annotation { "Feature Type Name" : "Feature", "Feature Type Description" : "" }
export const myFeature = defineFeature(function(context is Context, id is Id, definition is map)
    precondition{}
    {
        {
            var Q0;
            Q0=qCreatedBy(makeId("Top.planeOp"),FACE);
            var sketch = newSketch(context, id + "F0", { "sketchPlane" : qUnion([Q0])});
            skLineSegment(sketch, "E0.bottom", {"start": v(-40, 25) * mm, "end": v(40, 25) * mm});
            skLineSegment(sketch, "E0.top", {"start": v(-40, -25) * mm, "end": v(40, -25) * mm});
            skLineSegment(sketch, "E0.left", {"start": v(-40, 25) * mm, "end": v(-40, -25) * mm});
            skLineSegment(sketch, "E0.right", {"start": v(40, 25) * mm, "end": v(40, -25) * mm});
            skPoint(sketch, "E0.middle", {"position": v(0, 0) * mm});
            skSolve(sketch);
        }
        {
            var Q0;
            Q0 = qSketchRegion(id + "F0", true);
            extrude(context, id + "F1", {"entities" : qUnion([Q0]), "depth" : 100 * mm, "offsetDistance" : 25 * mm});
        }
        {
            var Q0;
            Q0=makeQuery(id+"F1.opExtrude","CAP_FACE",FACE,{"disambiguationData":[OSD([sQuery(id+"F0.wireOp",EDGE,"E0.bottom"),sQuery(id+"F0.wireOp",EDGE,"E0.top"),sQuery(id+"F0.wireOp",EDGE,"E0.left"),sQuery(id+"F0.wireOp",EDGE,"E0.right")])],"isStart":false});
            shell(context, id + "F2", {"entities" : qUnion([Q0]), "thickness" : 2.5 * mm});
        }
        {
            var Q0;
            Q0=makeQuery(id+"F1.opExtrude","CAP_FACE",FACE,{"disambiguationData":[OSD([sQuery(id+"F0.wireOp",EDGE,"E0.bottom"),sQuery(id+"F0.wireOp",EDGE,"E0.top"),sQuery(id+"F0.wireOp",EDGE,"E0.left"),sQuery(id+"F0.wireOp",EDGE,"E0.right")])],"isStart":true});
            var sketch = newSketch(context, id + "F3", { "sketchPlane" : qUnion([Q0])});
            skLineSegment(sketch, "E1", {"start": v(0, 19.4) * mm, "end": v(0, -22.73) * mm, "construction": true});
            skLineSegment(sketch, "E2", {"start": v(-35.25, 0) * mm, "end": v(36.43, 0) * mm, "construction": true});
            skLineSegment(sketch, "E3.bottom", {"start": v(-41, 26) * mm, "end": v(-11, 26) * mm});
            skLineSegment(sketch, "E3.top", {"start": v(-41, 6) * mm, "end": v(-11, 6) * mm});
            skLineSegment(sketch, "E3.left", {"start": v(-41, 26) * mm, "end": v(-41, 6) * mm});
            skLineSegment(sketch, "E3.right", {"start": v(-11, 26) * mm, "end": v(-11, 6) * mm});
            skLineSegment(sketch, "E4.bottom", {"start": v(-42, 27) * mm, "end": v(-16, 27) * mm});
            skLineSegment(sketch, "E4.top", {"start": v(-42, 11) * mm, "end": v(-16, 11) * mm});
            skLineSegment(sketch, "E4.left", {"start": v(-42, 27) * mm, "end": v(-42, 11) * mm});
            skLineSegment(sketch, "E4.right", {"start": v(-16, 27) * mm, "end": v(-16, 11) * mm});
            skLineSegment(sketch, "E5.bottom", {"start": v(-43, 28) * mm, "end": v(-21, 28) * mm});
            skLineSegment(sketch, "E5.top", {"start": v(-43, 16) * mm, "end": v(-21, 16) * mm});
            skLineSegment(sketch, "E5.left", {"start": v(-43, 28) * mm, "end": v(-43, 16) * mm});
            skLineSegment(sketch, "E5.right", {"start": v(-21, 28) * mm, "end": v(-21, 16) * mm});
            skLineSegment(sketch, "E6.MirrorCS", {"start": v(21, 28) * mm, "end": v(21, 16) * mm});
            skLineSegment(sketch, "E7.MirrorCS", {"start": v(41, 6) * mm, "end": v(11, 6) * mm});
            skLineSegment(sketch, "E8.MirrorCS", {"start": v(41, 26) * mm, "end": v(41, 6) * mm});
            skLineSegment(sketch, "E9.MirrorCS", {"start": v(11, 26) * mm, "end": v(11, 6) * mm});
            skLineSegment(sketch, "E10.MirrorCS", {"start": v(42, 27) * mm, "end": v(16, 27) * mm});
            skLineSegment(sketch, "E11.MirrorCS", {"start": v(42, 11) * mm, "end": v(16, 11) * mm});
            skLineSegment(sketch, "E12.MirrorCS", {"start": v(42, 27) * mm, "end": v(42, 11) * mm});
            skLineSegment(sketch, "E13.MirrorCS", {"start": v(41, 26) * mm, "end": v(11, 26) * mm});
            skLineSegment(sketch, "E14.MirrorCS", {"start": v(16, 27) * mm, "end": v(16, 11) * mm});
            skLineSegment(sketch, "E15.MirrorCS", {"start": v(43, 16) * mm, "end": v(21, 16) * mm});
            skLineSegment(sketch, "E16.MirrorCS", {"start": v(43, 28) * mm, "end": v(21, 28) * mm});
            skLineSegment(sketch, "E17.MirrorCS", {"start": v(43, 28) * mm, "end": v(43, 16) * mm});
            skLineSegment(sketch, "E18.MirrorCS", {"start": v(35.25, 0) * mm, "end": v(-36.43, 0) * mm, "construction": true});
            skLineSegment(sketch, "E19.MirrorCS", {"start": v(-21, -28) * mm, "end": v(-21, -16) * mm});
            skLineSegment(sketch, "E20.MirrorCS", {"start": v(-41, -26) * mm, "end": v(-11, -26) * mm});
            skLineSegment(sketch, "E21.MirrorCS", {"start": v(-41, -6) * mm, "end": v(-11, -6) * mm});
            skLineSegment(sketch, "E22.MirrorCS", {"start": v(-42, -27) * mm, "end": v(-16, -27) * mm});
            skLineSegment(sketch, "E23.MirrorCS", {"start": v(-11, -26) * mm, "end": v(-11, -6) * mm});
            skLineSegment(sketch, "E24.MirrorCS", {"start": v(-42, -11) * mm, "end": v(-16, -11) * mm});
            skLineSegment(sketch, "E25.MirrorCS", {"start": v(-42, -27) * mm, "end": v(-42, -11) * mm});
            skLineSegment(sketch, "E26.MirrorCS", {"start": v(-41, -26) * mm, "end": v(-41, -6) * mm});
            skLineSegment(sketch, "E27.MirrorCS", {"start": v(-16, -27) * mm, "end": v(-16, -11) * mm});
            skLineSegment(sketch, "E28.MirrorCS", {"start": v(-43, -28) * mm, "end": v(-21, -28) * mm});
            skLineSegment(sketch, "E29.MirrorCS", {"start": v(-43, -16) * mm, "end": v(-21, -16) * mm});
            skLineSegment(sketch, "E30.MirrorCS", {"start": v(-43, -28) * mm, "end": v(-43, -16) * mm});
            skLineSegment(sketch, "E31.MirrorCS", {"start": v(43, -28) * mm, "end": v(21, -28) * mm});
            skLineSegment(sketch, "E32.MirrorCS", {"start": v(41, -6) * mm, "end": v(11, -6) * mm});
            skLineSegment(sketch, "E33.MirrorCS", {"start": v(21, -28) * mm, "end": v(21, -16) * mm});
            skLineSegment(sketch, "E34.MirrorCS", {"start": v(42, -11) * mm, "end": v(16, -11) * mm});
            skLineSegment(sketch, "E35.MirrorCS", {"start": v(16, -27) * mm, "end": v(16, -11) * mm});
            skLineSegment(sketch, "E36.MirrorCS", {"start": v(41, -26) * mm, "end": v(41, -6) * mm});
            skLineSegment(sketch, "E37.MirrorCS", {"start": v(43, -28) * mm, "end": v(43, -16) * mm});
            skLineSegment(sketch, "E38.MirrorCS", {"start": v(11, -26) * mm, "end": v(11, -6) * mm});
            skLineSegment(sketch, "E39.MirrorCS", {"start": v(42, -27) * mm, "end": v(42, -11) * mm});
            skLineSegment(sketch, "E40.MirrorCS", {"start": v(42, -27) * mm, "end": v(16, -27) * mm});
            skLineSegment(sketch, "E41.MirrorCS", {"start": v(43, -16) * mm, "end": v(21, -16) * mm});
            skLineSegment(sketch, "E42.MirrorCS", {"start": v(41, -26) * mm, "end": v(11, -26) * mm});
            skSolve(sketch);
        }
        {
            var Q0;
            {var subQ1=sQuery(id+"F3.wireOp",EDGE,"E3.bottom");var subQ9=sQuery(id+"F3.wireOp",EDGE,"E3.left");var subQ11=makeQuery(id+"F3.imprint","INTERSECT",VERTEX,{"derivedFrom":[subQ1,subQ9]});Q0=makeQuery(id+"F3.imprint","IMPRINT",FACE,{"disambiguationData":[TD([[makeQuery(id+"F3.imprint","IMPRINT",EDGE,{"disambiguationData":[TD([[subQ11,-1.0]])],"derivedFrom":subQ1}),-1.0]])]});}
            var Q1;
            {var subQ0=sQuery(id+"F3.wireOp",EDGE,"E4.right");var subQ1=sQuery(id+"F3.wireOp",EDGE,"E3.bottom");var subQ2=makeQuery(id+"F3.imprint","INTERSECT",VERTEX,{"derivedFrom":[subQ1,subQ0]});Q1=makeQuery(id+"F3.imprint","IMPRINT",FACE,{"disambiguationData":[TD([[makeQuery(id+"F3.imprint","IMPRINT",EDGE,{"disambiguationData":[TD([[subQ2,1.0]])],"derivedFrom":subQ1}),-1.0]])]});}
            var Q2;
            {var subQ0=sQuery(id+"F3.wireOp",EDGE,"E3.right");var subQ1=sQuery(id+"F3.wireOp",EDGE,"E3.bottom");var subQ2=makeQuery(id+"F3.imprint","INTERSECT",VERTEX,{"derivedFrom":[subQ1,subQ0]});Q2=makeQuery(id+"F3.imprint","IMPRINT",FACE,{"disambiguationData":[TD([[makeQuery(id+"F3.imprint","IMPRINT",EDGE,{"disambiguationData":[TD([[subQ2,1.0]])],"derivedFrom":subQ1}),-1.0]])]});}
            var Q3;
            {var subQ0=sQuery(id+"F3.wireOp",EDGE,"E4.top");var subQ1=sQuery(id+"F3.wireOp",EDGE,"E3.left");var subQ2=makeQuery(id+"F3.imprint","INTERSECT",VERTEX,{"derivedFrom":[subQ1,subQ0]});Q3=makeQuery(id+"F3.imprint","IMPRINT",FACE,{"disambiguationData":[TD([[makeQuery(id+"F3.imprint","IMPRINT",EDGE,{"disambiguationData":[TD([[subQ2,1.0]])],"derivedFrom":subQ1}),1.0]])]});}
            var Q4;
            {var subQ0=sQuery(id+"F3.wireOp",EDGE,"E3.left");var subQ1=sQuery(id+"F3.wireOp",EDGE,"E3.top");var subQ2=makeQuery(id+"F3.imprint","INTERSECT",VERTEX,{"derivedFrom":[subQ1,subQ0]});Q4=makeQuery(id+"F3.imprint","IMPRINT",FACE,{"disambiguationData":[TD([[makeQuery(id+"F3.imprint","IMPRINT",EDGE,{"disambiguationData":[TD([[subQ2,-1.0]])],"derivedFrom":subQ1}),1.0]])]});}
            var Q5;
            {var subQ0=sQuery(id+"F3.wireOp",EDGE,"E26.MirrorCS");var subQ1=sQuery(id+"F3.wireOp",EDGE,"E21.MirrorCS");var subQ2=makeQuery(id+"F3.imprint","INTERSECT",VERTEX,{"derivedFrom":[subQ1,subQ0]});Q5=makeQuery(id+"F3.imprint","IMPRINT",FACE,{"disambiguationData":[TD([[makeQuery(id+"F3.imprint","IMPRINT",EDGE,{"disambiguationData":[TD([[subQ2,-1.0]])],"derivedFrom":subQ1}),-1.0]])]});}
            var Q6;
            {var subQ0=sQuery(id+"F3.wireOp",EDGE,"E26.MirrorCS");var subQ1=sQuery(id+"F3.wireOp",EDGE,"E24.MirrorCS");var subQ2=makeQuery(id+"F3.imprint","INTERSECT",VERTEX,{"derivedFrom":[subQ1,subQ0]});Q6=makeQuery(id+"F3.imprint","IMPRINT",FACE,{"disambiguationData":[TD([[makeQuery(id+"F3.imprint","IMPRINT",EDGE,{"disambiguationData":[TD([[subQ2,-1.0]])],"derivedFrom":subQ1}),-1.0]])]});}
            var Q7;
            {var subQ1=sQuery(id+"F3.wireOp",EDGE,"E20.MirrorCS");var subQ5=sQuery(id+"F3.wireOp",EDGE,"E19.MirrorCS");var subQ6=makeQuery(id+"F3.imprint","INTERSECT",VERTEX,{"derivedFrom":[subQ5,subQ1]});Q7=makeQuery(id+"F3.imprint","IMPRINT",FACE,{"disambiguationData":[TD([[makeQuery(id+"F3.imprint","IMPRINT",EDGE,{"disambiguationData":[TD([[subQ6,-1.0]])],"derivedFrom":subQ5}),1.0]])]});}
            var Q8;
            {var subQ0=sQuery(id+"F3.wireOp",EDGE,"E20.MirrorCS");var subQ1=sQuery(id+"F3.wireOp",EDGE,"E19.MirrorCS");var subQ2=makeQuery(id+"F3.imprint","INTERSECT",VERTEX,{"derivedFrom":[subQ1,subQ0]});Q8=makeQuery(id+"F3.imprint","IMPRINT",FACE,{"disambiguationData":[TD([[makeQuery(id+"F3.imprint","IMPRINT",EDGE,{"disambiguationData":[TD([[subQ2,-1.0]])],"derivedFrom":subQ1}),-1.0]])]});}
            var Q9;
            {var subQ0=sQuery(id+"F3.wireOp",EDGE,"E23.MirrorCS");var subQ1=sQuery(id+"F3.wireOp",EDGE,"E20.MirrorCS");var subQ2=makeQuery(id+"F3.imprint","INTERSECT",VERTEX,{"derivedFrom":[subQ1,subQ0]});Q9=makeQuery(id+"F3.imprint","IMPRINT",FACE,{"disambiguationData":[TD([[makeQuery(id+"F3.imprint","IMPRINT",EDGE,{"disambiguationData":[TD([[subQ2,1.0]])],"derivedFrom":subQ1}),1.0]])]});}
            var Q10;
            {var subQ0=sQuery(id+"F3.wireOp",EDGE,"E42.MirrorCS");var subQ1=sQuery(id+"F3.wireOp",EDGE,"E35.MirrorCS");var subQ2=makeQuery(id+"F3.imprint","INTERSECT",VERTEX,{"derivedFrom":[subQ1,subQ0]});Q10=makeQuery(id+"F3.imprint","IMPRINT",FACE,{"disambiguationData":[TD([[makeQuery(id+"F3.imprint","IMPRINT",EDGE,{"disambiguationData":[TD([[subQ2,-1.0]])],"derivedFrom":subQ1}),1.0]])]});}
            var Q11;
            {var subQ0=sQuery(id+"F3.wireOp",EDGE,"E42.MirrorCS");var subQ1=sQuery(id+"F3.wireOp",EDGE,"E33.MirrorCS");var subQ2=makeQuery(id+"F3.imprint","INTERSECT",VERTEX,{"derivedFrom":[subQ1,subQ0]});Q11=makeQuery(id+"F3.imprint","IMPRINT",FACE,{"disambiguationData":[TD([[makeQuery(id+"F3.imprint","IMPRINT",EDGE,{"disambiguationData":[TD([[subQ2,-1.0]])],"derivedFrom":subQ1}),1.0]])]});}
            var Q12;
            {var subQ0=sQuery(id+"F3.wireOp",EDGE,"E42.MirrorCS");var subQ3=sQuery(id+"F3.wireOp",EDGE,"E33.MirrorCS");var subQ4=makeQuery(id+"F3.imprint","INTERSECT",VERTEX,{"derivedFrom":[subQ3,subQ0]});Q12=makeQuery(id+"F3.imprint","IMPRINT",FACE,{"disambiguationData":[TD([[makeQuery(id+"F3.imprint","IMPRINT",EDGE,{"disambiguationData":[TD([[subQ4,-1.0]])],"derivedFrom":subQ3}),-1.0]])]});}
            var Q13;
            {var subQ0=sQuery(id+"F3.wireOp",EDGE,"E36.MirrorCS");var subQ1=sQuery(id+"F3.wireOp",EDGE,"E34.MirrorCS");var subQ2=makeQuery(id+"F3.imprint","INTERSECT",VERTEX,{"derivedFrom":[subQ1,subQ0]});Q13=makeQuery(id+"F3.imprint","IMPRINT",FACE,{"disambiguationData":[TD([[makeQuery(id+"F3.imprint","IMPRINT",EDGE,{"disambiguationData":[TD([[subQ2,-1.0]])],"derivedFrom":subQ1}),1.0]])]});}
            var Q14;
            {var subQ0=sQuery(id+"F3.wireOp",EDGE,"E36.MirrorCS");var subQ1=sQuery(id+"F3.wireOp",EDGE,"E32.MirrorCS");var subQ2=makeQuery(id+"F3.imprint","INTERSECT",VERTEX,{"derivedFrom":[subQ1,subQ0]});Q14=makeQuery(id+"F3.imprint","IMPRINT",FACE,{"disambiguationData":[TD([[makeQuery(id+"F3.imprint","IMPRINT",EDGE,{"disambiguationData":[TD([[subQ2,-1.0]])],"derivedFrom":subQ1}),1.0]])]});}
            var Q15;
            {var subQ0=sQuery(id+"F3.wireOp",EDGE,"E13.MirrorCS");var subQ1=sQuery(id+"F3.wireOp",EDGE,"E9.MirrorCS");var subQ2=makeQuery(id+"F3.imprint","INTERSECT",VERTEX,{"derivedFrom":[subQ1,subQ0]});Q15=makeQuery(id+"F3.imprint","IMPRINT",FACE,{"disambiguationData":[TD([[makeQuery(id+"F3.imprint","IMPRINT",EDGE,{"disambiguationData":[TD([[subQ2,-1.0]])],"derivedFrom":subQ1}),1.0]])]});}
            var Q16;
            {var subQ0=sQuery(id+"F3.wireOp",EDGE,"E13.MirrorCS");var subQ1=sQuery(id+"F3.wireOp",EDGE,"E6.MirrorCS");var subQ2=makeQuery(id+"F3.imprint","INTERSECT",VERTEX,{"derivedFrom":[subQ1,subQ0]});Q16=makeQuery(id+"F3.imprint","IMPRINT",FACE,{"disambiguationData":[TD([[makeQuery(id+"F3.imprint","IMPRINT",EDGE,{"disambiguationData":[TD([[subQ2,-1.0]])],"derivedFrom":subQ1}),-1.0]])]});}
            var Q17;
            {var subQ0=sQuery(id+"F3.wireOp",EDGE,"E13.MirrorCS");var subQ3=sQuery(id+"F3.wireOp",EDGE,"E6.MirrorCS");var subQ4=makeQuery(id+"F3.imprint","INTERSECT",VERTEX,{"derivedFrom":[subQ3,subQ0]});Q17=makeQuery(id+"F3.imprint","IMPRINT",FACE,{"disambiguationData":[TD([[makeQuery(id+"F3.imprint","IMPRINT",EDGE,{"disambiguationData":[TD([[subQ4,-1.0]])],"derivedFrom":subQ3}),1.0]])]});}
            var Q18;
            {var subQ0=sQuery(id+"F3.wireOp",EDGE,"E11.MirrorCS");var subQ1=sQuery(id+"F3.wireOp",EDGE,"E8.MirrorCS");var subQ2=makeQuery(id+"F3.imprint","INTERSECT",VERTEX,{"derivedFrom":[subQ1,subQ0]});Q18=makeQuery(id+"F3.imprint","IMPRINT",FACE,{"disambiguationData":[TD([[makeQuery(id+"F3.imprint","IMPRINT",EDGE,{"disambiguationData":[TD([[subQ2,1.0]])],"derivedFrom":subQ1}),-1.0]])]});}
            var Q19;
            {var subQ0=sQuery(id+"F3.wireOp",EDGE,"E8.MirrorCS");var subQ1=sQuery(id+"F3.wireOp",EDGE,"E7.MirrorCS");var subQ2=makeQuery(id+"F3.imprint","INTERSECT",VERTEX,{"derivedFrom":[subQ1,subQ0]});Q19=makeQuery(id+"F3.imprint","IMPRINT",FACE,{"disambiguationData":[TD([[makeQuery(id+"F3.imprint","IMPRINT",EDGE,{"disambiguationData":[TD([[subQ2,-1.0]])],"derivedFrom":subQ1}),-1.0]])]});}
            extrude(context, id + "F4", {"entities" : qUnion([Q0, Q1, Q2, Q3, Q4, Q5, Q6, Q7, Q8, Q9, Q10, Q11, Q12, Q13, Q14, Q15, Q16, Q17, Q18, Q19]), "operationType" : NewBodyOperationType.ADD, "oppositeDirection" : true, "depth" : 75 * mm, "offsetDistance" : 25 * mm});
        }
        {
            var Q0;
            {var subQ0=sQuery(id+"F3.wireOp",EDGE,"E4.top");var subQ1=sQuery(id+"F3.wireOp",EDGE,"E3.left");var subQ2=makeQuery(id+"F3.imprint","INTERSECT",VERTEX,{"derivedFrom":[subQ1,subQ0]});Q0=makeQuery(id+"F3.imprint","IMPRINT",FACE,{"disambiguationData":[TD([[makeQuery(id+"F3.imprint","IMPRINT",EDGE,{"disambiguationData":[TD([[subQ2,1.0]])],"derivedFrom":subQ1}),-1.0]])]});}
            var Q1;
            {var subQ7=sQuery(id+"F3.wireOp",EDGE,"E3.left");var subQ8=sQuery(id+"F3.wireOp",EDGE,"E3.bottom");var subQ9=makeQuery(id+"F3.imprint","INTERSECT",VERTEX,{"derivedFrom":[subQ8,subQ7]});Q1=makeQuery(id+"F3.imprint","IMPRINT",FACE,{"disambiguationData":[TD([[makeQuery(id+"F3.imprint","IMPRINT",EDGE,{"disambiguationData":[TD([[subQ9,-1.0]])],"derivedFrom":subQ8}),1.0]])]});}
            var Q2;
            {var subQ0=sQuery(id+"F3.wireOp",EDGE,"E4.right");var subQ1=sQuery(id+"F3.wireOp",EDGE,"E3.bottom");var subQ2=makeQuery(id+"F3.imprint","INTERSECT",VERTEX,{"derivedFrom":[subQ1,subQ0]});Q2=makeQuery(id+"F3.imprint","IMPRINT",FACE,{"disambiguationData":[TD([[makeQuery(id+"F3.imprint","IMPRINT",EDGE,{"disambiguationData":[TD([[subQ2,1.0]])],"derivedFrom":subQ1}),1.0]])]});}
            var Q3;
            {var subQ0=sQuery(id+"F3.wireOp",EDGE,"E10.MirrorCS");var subQ1=sQuery(id+"F3.wireOp",EDGE,"E6.MirrorCS");var subQ2=makeQuery(id+"F3.imprint","INTERSECT",VERTEX,{"derivedFrom":[subQ1,subQ0]});Q3=makeQuery(id+"F3.imprint","IMPRINT",FACE,{"disambiguationData":[TD([[makeQuery(id+"F3.imprint","IMPRINT",EDGE,{"disambiguationData":[TD([[subQ2,-1.0]])],"derivedFrom":subQ1}),-1.0]])]});}
            var Q4;
            {var subQ1=sQuery(id+"F3.wireOp",EDGE,"E10.MirrorCS");var subQ5=sQuery(id+"F3.wireOp",EDGE,"E6.MirrorCS");var subQ6=makeQuery(id+"F3.imprint","INTERSECT",VERTEX,{"derivedFrom":[subQ5,subQ1]});Q4=makeQuery(id+"F3.imprint","IMPRINT",FACE,{"disambiguationData":[TD([[makeQuery(id+"F3.imprint","IMPRINT",EDGE,{"disambiguationData":[TD([[subQ6,-1.0]])],"derivedFrom":subQ5}),1.0]])]});}
            var Q5;
            {var subQ0=sQuery(id+"F3.wireOp",EDGE,"E11.MirrorCS");var subQ1=sQuery(id+"F3.wireOp",EDGE,"E8.MirrorCS");var subQ2=makeQuery(id+"F3.imprint","INTERSECT",VERTEX,{"derivedFrom":[subQ1,subQ0]});Q5=makeQuery(id+"F3.imprint","IMPRINT",FACE,{"disambiguationData":[TD([[makeQuery(id+"F3.imprint","IMPRINT",EDGE,{"disambiguationData":[TD([[subQ2,1.0]])],"derivedFrom":subQ1}),1.0]])]});}
            var Q6;
            {var subQ0=sQuery(id+"F3.wireOp",EDGE,"E39.MirrorCS");var subQ1=sQuery(id+"F3.wireOp",EDGE,"E34.MirrorCS");var subQ2=makeQuery(id+"F3.imprint","INTERSECT",VERTEX,{"derivedFrom":[subQ1,subQ0]});Q6=makeQuery(id+"F3.imprint","IMPRINT",FACE,{"disambiguationData":[TD([[makeQuery(id+"F3.imprint","IMPRINT",EDGE,{"disambiguationData":[TD([[subQ2,-1.0]])],"derivedFrom":subQ1}),1.0]])]});}
            var Q7;
            {var subQ0=sQuery(id+"F3.wireOp",EDGE,"E40.MirrorCS");var subQ3=sQuery(id+"F3.wireOp",EDGE,"E33.MirrorCS");var subQ4=makeQuery(id+"F3.imprint","INTERSECT",VERTEX,{"derivedFrom":[subQ3,subQ0]});Q7=makeQuery(id+"F3.imprint","IMPRINT",FACE,{"disambiguationData":[TD([[makeQuery(id+"F3.imprint","IMPRINT",EDGE,{"disambiguationData":[TD([[subQ4,-1.0]])],"derivedFrom":subQ3}),-1.0]])]});}
            var Q8;
            {var subQ0=sQuery(id+"F3.wireOp",EDGE,"E40.MirrorCS");var subQ1=sQuery(id+"F3.wireOp",EDGE,"E33.MirrorCS");var subQ2=makeQuery(id+"F3.imprint","INTERSECT",VERTEX,{"derivedFrom":[subQ1,subQ0]});Q8=makeQuery(id+"F3.imprint","IMPRINT",FACE,{"disambiguationData":[TD([[makeQuery(id+"F3.imprint","IMPRINT",EDGE,{"disambiguationData":[TD([[subQ2,-1.0]])],"derivedFrom":subQ1}),1.0]])]});}
            var Q9;
            {var subQ0=sQuery(id+"F3.wireOp",EDGE,"E25.MirrorCS");var subQ1=sQuery(id+"F3.wireOp",EDGE,"E24.MirrorCS");var subQ2=makeQuery(id+"F3.imprint","INTERSECT",VERTEX,{"derivedFrom":[subQ1,subQ0]});Q9=makeQuery(id+"F3.imprint","IMPRINT",FACE,{"disambiguationData":[TD([[makeQuery(id+"F3.imprint","IMPRINT",EDGE,{"disambiguationData":[TD([[subQ2,-1.0]])],"derivedFrom":subQ1}),-1.0]])]});}
            var Q10;
            {var subQ1=sQuery(id+"F3.wireOp",EDGE,"E22.MirrorCS");var subQ3=sQuery(id+"F3.wireOp",EDGE,"E19.MirrorCS");var subQ4=makeQuery(id+"F3.imprint","INTERSECT",VERTEX,{"derivedFrom":[subQ3,subQ1]});Q10=makeQuery(id+"F3.imprint","IMPRINT",FACE,{"disambiguationData":[TD([[makeQuery(id+"F3.imprint","IMPRINT",EDGE,{"disambiguationData":[TD([[subQ4,-1.0]])],"derivedFrom":subQ3}),1.0]])]});}
            var Q11;
            {var subQ0=sQuery(id+"F3.wireOp",EDGE,"E22.MirrorCS");var subQ1=sQuery(id+"F3.wireOp",EDGE,"E19.MirrorCS");var subQ2=makeQuery(id+"F3.imprint","INTERSECT",VERTEX,{"derivedFrom":[subQ1,subQ0]});Q11=makeQuery(id+"F3.imprint","IMPRINT",FACE,{"disambiguationData":[TD([[makeQuery(id+"F3.imprint","IMPRINT",EDGE,{"disambiguationData":[TD([[subQ2,-1.0]])],"derivedFrom":subQ1}),-1.0]])]});}
            extrude(context, id + "F5", {"entities" : qUnion([Q0, Q1, Q2, Q3, Q4, Q5, Q6, Q7, Q8, Q9, Q10, Q11]), "operationType" : NewBodyOperationType.ADD, "oppositeDirection" : true, "depth" : 65 * mm, "offsetDistance" : 25 * mm});
        }
        {
            var Q0;
            {var subQ5=sQuery(id+"F3.wireOp",EDGE,"E28.MirrorCS");Q0=makeQuery(id+"F3.imprint","IMPRINT",FACE,{"disambiguationData":[TD([[makeQuery(id+"F3.imprint","IMPRINT",EDGE,{"derivedFrom":subQ5}),1.0]])]});}
            var Q1;
            {var subQ8=sQuery(id+"F3.wireOp",EDGE,"E5.bottom");Q1=makeQuery(id+"F3.imprint","IMPRINT",FACE,{"disambiguationData":[TD([[makeQuery(id+"F3.imprint","IMPRINT",EDGE,{"derivedFrom":subQ8}),-1.0]])]});}
            var Q2;
            {var subQ8=sQuery(id+"F3.wireOp",EDGE,"E16.MirrorCS");Q2=makeQuery(id+"F3.imprint","IMPRINT",FACE,{"disambiguationData":[TD([[makeQuery(id+"F3.imprint","IMPRINT",EDGE,{"derivedFrom":subQ8}),1.0]])]});}
            var Q3;
            {var subQ7=sQuery(id+"F3.wireOp",EDGE,"E31.MirrorCS");Q3=makeQuery(id+"F3.imprint","IMPRINT",FACE,{"disambiguationData":[TD([[makeQuery(id+"F3.imprint","IMPRINT",EDGE,{"derivedFrom":subQ7}),-1.0]])]});}
            extrude(context, id + "F6", {"entities" : qUnion([Q0, Q1, Q2, Q3]), "operationType" : NewBodyOperationType.ADD, "oppositeDirection" : true, "depth" : 55 * mm, "offsetDistance" : 25 * mm});
        }
        {
            var Q0;
            Q0=makeQuery(id+"F1.opExtrude","CAP_FACE",FACE,{"disambiguationData":[OSD([sQuery(id+"F0.wireOp",EDGE,"E0.bottom"),sQuery(id+"F0.wireOp",EDGE,"E0.top"),sQuery(id+"F0.wireOp",EDGE,"E0.left"),sQuery(id+"F0.wireOp",EDGE,"E0.right")])],"isStart":false});
            var sketch = newSketch(context, id + "F7", { "sketchPlane" : qUnion([Q0])});
            skLineSegment(sketch, "E43.top", {"start": v(-40, 6) * mm, "end": v(-39, 6) * mm});
            skLineSegment(sketch, "E43.left", {"start": v(-40, 25) * mm, "end": v(-40, 6) * mm});
            skLineSegment(sketch, "E43.right", {"start": v(-39, 24) * mm, "end": v(-39, 6) * mm});
            skLineSegment(sketch, "E44.bottom", {"start": v(-40, 25) * mm, "end": v(-11, 25) * mm});
            skLineSegment(sketch, "E44.top", {"start": v(-39, 24) * mm, "end": v(-11, 24) * mm});
            skLineSegment(sketch, "E44.right", {"start": v(-11, 25) * mm, "end": v(-11, 24) * mm});
            skLineSegment(sketch, "E45", {"start": v(0, 29.1) * mm, "end": v(0, -30.85) * mm, "construction": true});
            skPoint(sketch, "E45.startSnap0", {"position": v(0, 25) * mm});
            skLineSegment(sketch, "E46", {"start": v(-50.1, 0) * mm, "end": v(60.67, 0) * mm, "construction": true});
            skLineSegment(sketch, "E47.MirrorCS", {"start": v(40, 6) * mm, "end": v(39, 6) * mm});
            skLineSegment(sketch, "E48.MirrorCS", {"start": v(11, 25) * mm, "end": v(11, 24) * mm});
            skLineSegment(sketch, "E49.MirrorCS", {"start": v(40, 25) * mm, "end": v(11, 25) * mm});
            skLineSegment(sketch, "E50.MirrorCS", {"start": v(40, 25) * mm, "end": v(40, 6) * mm});
            skLineSegment(sketch, "E51.MirrorCS", {"start": v(39, 24) * mm, "end": v(11, 24) * mm});
            skLineSegment(sketch, "E52.MirrorCS", {"start": v(39, 24) * mm, "end": v(39, 6) * mm});
            skLineSegment(sketch, "E53.MirrorCS", {"start": v(-40, -6) * mm, "end": v(-39, -6) * mm});
            skLineSegment(sketch, "E54.MirrorCS", {"start": v(11, -25) * mm, "end": v(11, -24) * mm});
            skLineSegment(sketch, "E55.MirrorCS", {"start": v(40, -6) * mm, "end": v(39, -6) * mm});
            skLineSegment(sketch, "E56.MirrorCS", {"start": v(-11, -25) * mm, "end": v(-11, -24) * mm});
            skLineSegment(sketch, "E57.MirrorCS", {"start": v(-40, -25) * mm, "end": v(-40, -6) * mm});
            skLineSegment(sketch, "E58.MirrorCS", {"start": v(39, -24) * mm, "end": v(39, -6) * mm});
            skPoint(sketch, "E59.MirrorP", {"position": v(0, -25) * mm});
            skLineSegment(sketch, "E60.MirrorCS", {"start": v(40, -25) * mm, "end": v(11, -25) * mm});
            skLineSegment(sketch, "E61.MirrorCS", {"start": v(-39, -24) * mm, "end": v(-39, -6) * mm});
            skLineSegment(sketch, "E62.MirrorCS", {"start": v(-40, -25) * mm, "end": v(-11, -25) * mm});
            skLineSegment(sketch, "E63.MirrorCS", {"start": v(-39, -24) * mm, "end": v(-11, -24) * mm});
            skLineSegment(sketch, "E64.MirrorCS", {"start": v(39, -24) * mm, "end": v(11, -24) * mm});
            skLineSegment(sketch, "E65.MirrorCS", {"start": v(40, -25) * mm, "end": v(40, -6) * mm});
            skSolve(sketch);
        }
        {
            var Q0;
            Q0 = qSketchRegion(id + "F7", true);
            extrude(context, id + "F8", {"entities" : qUnion([Q0]), "operationType" : NewBodyOperationType.REMOVE, "oppositeDirection" : true, "depth" : 15 * mm, "offsetDistance" : 25 * mm});
        }
        {
            var Q0;
            Q0=makeQuery(id+"F1.opExtrude","SWEPT_FACE",FACE,{"disambiguationData":[OSD([sQuery(id+"F0.wireOp",EDGE,"E0.bottom")])]});
            var sketch = newSketch(context, id + "F9", { "sketchPlane" : qUnion([Q0])});
            skLineSegment(sketch, "E66.bottom", {"start": v(-7.75, 95) * mm, "end": v(-5.25, 95) * mm});
            skLineSegment(sketch, "E66.top", {"start": v(-7.75, 5) * mm, "end": v(-5.25, 5) * mm});
            skLineSegment(sketch, "E66.left", {"start": v(-7.75, 95) * mm, "end": v(-7.75, 5) * mm});
            skLineSegment(sketch, "E66.right", {"start": v(-5.25, 95) * mm, "end": v(-5.25, 5) * mm});
            skLineSegment(sketch, "E67.bottom", {"start": v(-1.25, 95) * mm, "end": v(1.25, 95) * mm});
            skLineSegment(sketch, "E67.top", {"start": v(-1.25, 5) * mm, "end": v(1.25, 5) * mm});
            skLineSegment(sketch, "E67.left", {"start": v(-1.25, 95) * mm, "end": v(-1.25, 5) * mm});
            skLineSegment(sketch, "E67.right", {"start": v(1.25, 95) * mm, "end": v(1.25, 5) * mm});
            skLineSegment(sketch, "E68.bottom", {"start": v(5.25, 5) * mm, "end": v(7.75, 5) * mm});
            skLineSegment(sketch, "E68.top", {"start": v(5.25, 95) * mm, "end": v(7.75, 95) * mm});
            skLineSegment(sketch, "E68.left", {"start": v(5.25, 5) * mm, "end": v(5.25, 95) * mm});
            skLineSegment(sketch, "E68.right", {"start": v(7.75, 5) * mm, "end": v(7.75, 95) * mm});
            skSolve(sketch);
        }
        {
            var Q0;
            Q0 = qSketchRegion(id + "F9", true);
            extrude(context, id + "F10", {"entities" : qUnion([Q0]), "operationType" : NewBodyOperationType.REMOVE, "oppositeDirection" : true, "depth" : 1 * mm, "offsetDistance" : 25 * mm});
        }
        {
            var Q0;
            Q0=makeQuery(id+"F1.opExtrude","SWEPT_FACE",FACE,{"disambiguationData":[OSD([sQuery(id+"F0.wireOp",EDGE,"E0.top")])]});
            var sketch = newSketch(context, id + "F11", { "sketchPlane" : qUnion([Q0])});
            skLineSegment(sketch, "E69.bottom", {"start": v(-7.75, 95) * mm, "end": v(-5.25, 95) * mm});
            skLineSegment(sketch, "E69.top", {"start": v(-7.75, 5) * mm, "end": v(-5.25, 5) * mm});
            skLineSegment(sketch, "E69.left", {"start": v(-7.75, 95) * mm, "end": v(-7.75, 5) * mm});
            skLineSegment(sketch, "E69.right", {"start": v(-5.25, 95) * mm, "end": v(-5.25, 5) * mm});
            skLineSegment(sketch, "E70.bottom", {"start": v(-1.25, 5) * mm, "end": v(1.25, 5) * mm});
            skLineSegment(sketch, "E70.top", {"start": v(-1.25, 95) * mm, "end": v(1.25, 95) * mm});
            skLineSegment(sketch, "E70.left", {"start": v(-1.25, 5) * mm, "end": v(-1.25, 95) * mm});
            skLineSegment(sketch, "E70.right", {"start": v(1.25, 5) * mm, "end": v(1.25, 95) * mm});
            skLineSegment(sketch, "E71.bottom", {"start": v(5.25, 95) * mm, "end": v(7.75, 95) * mm});
            skLineSegment(sketch, "E71.top", {"start": v(5.25, 5) * mm, "end": v(7.75, 5) * mm});
            skLineSegment(sketch, "E71.left", {"start": v(5.25, 95) * mm, "end": v(5.25, 5) * mm});
            skLineSegment(sketch, "E71.right", {"start": v(7.75, 95) * mm, "end": v(7.75, 5) * mm});
            skSolve(sketch);
        }
        {
            var Q0;
            Q0 = qSketchRegion(id + "F11", true);
            extrude(context, id + "F12", {"entities" : qUnion([Q0]), "operationType" : NewBodyOperationType.REMOVE, "oppositeDirection" : true, "depth" : 1 * mm, "offsetDistance" : 25 * mm});
        }
        {
            var Q0;
            Q0=makeQuery(id+"F1.opExtrude","SWEPT_FACE",FACE,{"disambiguationData":[OSD([sQuery(id+"F0.wireOp",EDGE,"E0.left")])]});
            var sketch = newSketch(context, id + "F13", { "sketchPlane" : qUnion([Q0])});
            skLineSegment(sketch, "E72.bottom", {"start": v(-1.25, 95) * mm, "end": v(1.25, 95) * mm});
            skLineSegment(sketch, "E72.top", {"start": v(-1.25, 5) * mm, "end": v(1.25, 5) * mm});
            skLineSegment(sketch, "E72.left", {"start": v(-1.25, 95) * mm, "end": v(-1.25, 5) * mm});
            skLineSegment(sketch, "E72.right", {"start": v(1.25, 95) * mm, "end": v(1.25, 5) * mm});
            skLineSegment(sketch, "E73", {"start": v(-1.25, 15) * mm, "end": v(1.25, 15) * mm});
            skLineSegment(sketch, "E74.0.1.0", {"start": v(-1.25, 25) * mm, "end": v(1.25, 25) * mm});
            skLineSegment(sketch, "E74.0.2.0", {"start": v(-1.25, 35) * mm, "end": v(1.25, 35) * mm});
            skLineSegment(sketch, "E74.0.3.0", {"start": v(-1.25, 45) * mm, "end": v(1.25, 45) * mm});
            skLineSegment(sketch, "E74.0.4.0", {"start": v(-1.25, 55) * mm, "end": v(1.25, 55) * mm});
            skLineSegment(sketch, "E74.0.5.0", {"start": v(-1.25, 65) * mm, "end": v(1.25, 65) * mm});
            skLineSegment(sketch, "E74.0.6.0", {"start": v(-1.25, 75) * mm, "end": v(1.25, 75) * mm});
            skLineSegment(sketch, "E74.0.7.0", {"start": v(-1.25, 85) * mm, "end": v(1.25, 85) * mm});
            skLineSegment(sketch, "E74.direction1", {"start": v(-1.25, 15) * mm, "end": v(23.75, 15) * mm, "construction": true});
            skLineSegment(sketch, "E74.direction2", {"start": v(-1.25, 15) * mm, "end": v(-1.25, 25) * mm, "construction": true});
            skSolve(sketch);
        }
        {
            var Q0;
            {var subQ0=sQuery(id+"F13.wireOp",EDGE,"E72.bottom");Q0=makeQuery(id+"F13.imprint","IMPRINT",FACE,{"disambiguationData":[TD([[makeQuery(id+"F13.imprint","IMPRINT",EDGE,{"derivedFrom":subQ0}),-1.0]])]});}
            var Q1;
            {var subQ0=sQuery(id+"F13.wireOp",EDGE,"E74.0.5.0");Q1=makeQuery(id+"F13.imprint","IMPRINT",FACE,{"disambiguationData":[TD([[makeQuery(id+"F13.imprint","IMPRINT",EDGE,{"derivedFrom":subQ0}),1.0]])]});}
            var Q2;
            {var subQ0=sQuery(id+"F13.wireOp",EDGE,"E74.0.3.0");Q2=makeQuery(id+"F13.imprint","IMPRINT",FACE,{"disambiguationData":[TD([[makeQuery(id+"F13.imprint","IMPRINT",EDGE,{"derivedFrom":subQ0}),1.0]])]});}
            var Q3;
            {var subQ0=sQuery(id+"F13.wireOp",EDGE,"E74.0.1.0");Q3=makeQuery(id+"F13.imprint","IMPRINT",FACE,{"disambiguationData":[TD([[makeQuery(id+"F13.imprint","IMPRINT",EDGE,{"derivedFrom":subQ0}),1.0]])]});}
            var Q4;
            {var subQ0=sQuery(id+"F13.wireOp",EDGE,"E72.top");Q4=makeQuery(id+"F13.imprint","IMPRINT",FACE,{"disambiguationData":[TD([[makeQuery(id+"F13.imprint","IMPRINT",EDGE,{"derivedFrom":subQ0}),1.0]])]});}
            extrude(context, id + "F14", {"entities" : qUnion([Q0, Q1, Q2, Q3, Q4]), "operationType" : NewBodyOperationType.REMOVE, "oppositeDirection" : true, "depth" : 1 * mm, "offsetDistance" : 25 * mm});
        }
        {
            var Q0;
            Q0=makeQuery(id+"F1.opExtrude","SWEPT_FACE",FACE,{"disambiguationData":[OSD([sQuery(id+"F0.wireOp",EDGE,"E0.right")])]});
            var sketch = newSketch(context, id + "F15", { "sketchPlane" : qUnion([Q0])});
            skLineSegment(sketch, "E75.bottom", {"start": v(-1.25, 95) * mm, "end": v(1.25, 95) * mm});
            skLineSegment(sketch, "E75.top", {"start": v(-1.25, 5) * mm, "end": v(1.25, 5) * mm});
            skLineSegment(sketch, "E75.left", {"start": v(-1.25, 95) * mm, "end": v(-1.25, 5) * mm});
            skLineSegment(sketch, "E75.right", {"start": v(1.25, 95) * mm, "end": v(1.25, 5) * mm});
            skLineSegment(sketch, "E76", {"start": v(-1.25, 15) * mm, "end": v(1.25, 15) * mm});
            skLineSegment(sketch, "E77.0.1.0", {"start": v(-1.25, 25) * mm, "end": v(1.25, 25) * mm});
            skLineSegment(sketch, "E77.0.2.0", {"start": v(-1.25, 35) * mm, "end": v(1.25, 35) * mm});
            skLineSegment(sketch, "E77.0.3.0", {"start": v(-1.25, 45) * mm, "end": v(1.25, 45) * mm});
            skLineSegment(sketch, "E77.0.4.0", {"start": v(-1.25, 55) * mm, "end": v(1.25, 55) * mm});
            skLineSegment(sketch, "E77.0.5.0", {"start": v(-1.25, 65) * mm, "end": v(1.25, 65) * mm});
            skLineSegment(sketch, "E77.0.6.0", {"start": v(-1.25, 75) * mm, "end": v(1.25, 75) * mm});
            skLineSegment(sketch, "E77.0.7.0", {"start": v(-1.25, 85) * mm, "end": v(1.25, 85) * mm});
            skLineSegment(sketch, "E77.direction1", {"start": v(-1.25, 15) * mm, "end": v(23.75, 15) * mm, "construction": true});
            skLineSegment(sketch, "E77.direction2", {"start": v(-1.25, 15) * mm, "end": v(-1.25, 25) * mm, "construction": true});
            skSolve(sketch);
        }
        {
            var Q0;
            {var subQ0=sQuery(id+"F15.wireOp",EDGE,"E75.bottom");Q0=makeQuery(id+"F15.imprint","IMPRINT",FACE,{"disambiguationData":[TD([[makeQuery(id+"F15.imprint","IMPRINT",EDGE,{"derivedFrom":subQ0}),-1.0]])]});}
            var Q1;
            {var subQ0=sQuery(id+"F15.wireOp",EDGE,"E77.0.5.0");Q1=makeQuery(id+"F15.imprint","IMPRINT",FACE,{"disambiguationData":[TD([[makeQuery(id+"F15.imprint","IMPRINT",EDGE,{"derivedFrom":subQ0}),1.0]])]});}
            var Q2;
            {var subQ0=sQuery(id+"F15.wireOp",EDGE,"E77.0.3.0");Q2=makeQuery(id+"F15.imprint","IMPRINT",FACE,{"disambiguationData":[TD([[makeQuery(id+"F15.imprint","IMPRINT",EDGE,{"derivedFrom":subQ0}),1.0]])]});}
            var Q3;
            {var subQ0=sQuery(id+"F15.wireOp",EDGE,"E77.0.1.0");Q3=makeQuery(id+"F15.imprint","IMPRINT",FACE,{"disambiguationData":[TD([[makeQuery(id+"F15.imprint","IMPRINT",EDGE,{"derivedFrom":subQ0}),1.0]])]});}
            var Q4;
            {var subQ0=sQuery(id+"F15.wireOp",EDGE,"E75.top");Q4=makeQuery(id+"F15.imprint","IMPRINT",FACE,{"disambiguationData":[TD([[makeQuery(id+"F15.imprint","IMPRINT",EDGE,{"derivedFrom":subQ0}),1.0]])]});}
            extrude(context, id + "F16", {"entities" : qUnion([Q0, Q1, Q2, Q3, Q4]), "operationType" : NewBodyOperationType.REMOVE, "oppositeDirection" : true, "depth" : 1 * mm, "offsetDistance" : 25 * mm});
        }
        {
            var Q0;
            {var subQ0=sQuery(id+"F3.wireOp",EDGE,"E40.MirrorCS");var subQ1=sQuery(id+"F3.wireOp",EDGE,"E39.MirrorCS");var subQ2=sQuery(id+"F3.wireOp",EDGE,"E25.MirrorCS");var subQ3=sQuery(id+"F3.wireOp",EDGE,"E22.MirrorCS");var subQ4=sQuery(id+"F3.wireOp",EDGE,"E12.MirrorCS");var subQ5=sQuery(id+"F3.wireOp",EDGE,"E10.MirrorCS");var subQ6=sQuery(id+"F3.wireOp",EDGE,"E4.left");var subQ7=sQuery(id+"F3.wireOp",EDGE,"E4.bottom");var subQ8=sQuery(id+"F3.wireOp",EDGE,"E42.MirrorCS");var subQ9=sQuery(id+"F3.wireOp",EDGE,"E36.MirrorCS");var subQ10=sQuery(id+"F3.wireOp",EDGE,"E26.MirrorCS");var subQ11=sQuery(id+"F3.wireOp",EDGE,"E20.MirrorCS");var subQ12=sQuery(id+"F3.wireOp",EDGE,"E13.MirrorCS");var subQ13=sQuery(id+"F3.wireOp",EDGE,"E8.MirrorCS");var subQ14=sQuery(id+"F3.wireOp",EDGE,"E3.left");var subQ15=sQuery(id+"F3.wireOp",EDGE,"E3.bottom");var subQ16=sQuery(id+"F0.wireOp",EDGE,"E0.right");var subQ17=sQuery(id+"F0.wireOp",EDGE,"E0.bottom");var subQ18=sQuery(id+"F0.wireOp",EDGE,"E0.left");var subQ19=sQuery(id+"F0.wireOp",EDGE,"E0.top");Q0=makeQuery(id+"F6.boolean.opBoolean","MERGE",FACE,{"derivedFrom":[makeQuery(id+"F5.boolean.opBoolean","MERGE",FACE,{"derivedFrom":[makeQuery(id+"F4.boolean.opBoolean","MERGE",FACE,{"derivedFrom":[makeQuery(id+"F1.opExtrude","CAP_FACE",FACE,{"disambiguationData":[OSD([subQ17,subQ19,subQ18,subQ16])],"isStart":true}),makeQuery(id+"F4.opExtrude","CAP_FACE",FACE,{"disambiguationData":[OSD([subQ19,subQ18,subQ15,sQuery(id+"F3.wireOp",EDGE,"E3.top"),subQ14,sQuery(id+"F3.wireOp",EDGE,"E3.right")])],"isStart":true}),makeQuery(id+"F4.opExtrude","CAP_FACE",FACE,{"disambiguationData":[OSD([subQ19,subQ16,sQuery(id+"F3.wireOp",EDGE,"E7.MirrorCS"),subQ13,sQuery(id+"F3.wireOp",EDGE,"E9.MirrorCS"),subQ12])],"isStart":true}),makeQuery(id+"F4.opExtrude","CAP_FACE",FACE,{"disambiguationData":[OSD([subQ17,subQ18,subQ11,sQuery(id+"F3.wireOp",EDGE,"E21.MirrorCS"),sQuery(id+"F3.wireOp",EDGE,"E23.MirrorCS"),subQ10])],"isStart":true}),makeQuery(id+"F4.opExtrude","CAP_FACE",FACE,{"disambiguationData":[OSD([subQ17,subQ16,sQuery(id+"F3.wireOp",EDGE,"E32.MirrorCS"),subQ9,sQuery(id+"F3.wireOp",EDGE,"E38.MirrorCS"),subQ8])],"isStart":true})]}),makeQuery(id+"F5.opExtrude","CAP_FACE",FACE,{"disambiguationData":[OSD([subQ15,subQ14,subQ7,sQuery(id+"F3.wireOp",EDGE,"E4.top"),subQ6,sQuery(id+"F3.wireOp",EDGE,"E4.right")])],"isStart":true}),makeQuery(id+"F5.opExtrude","CAP_FACE",FACE,{"disambiguationData":[OSD([subQ13,subQ5,sQuery(id+"F3.wireOp",EDGE,"E11.MirrorCS"),subQ4,subQ12,sQuery(id+"F3.wireOp",EDGE,"E14.MirrorCS")])],"isStart":true}),makeQuery(id+"F5.opExtrude","CAP_FACE",FACE,{"disambiguationData":[OSD([subQ11,subQ3,sQuery(id+"F3.wireOp",EDGE,"E24.MirrorCS"),subQ2,subQ10,sQuery(id+"F3.wireOp",EDGE,"E27.MirrorCS")])],"isStart":true}),makeQuery(id+"F5.opExtrude","CAP_FACE",FACE,{"disambiguationData":[OSD([sQuery(id+"F3.wireOp",EDGE,"E34.MirrorCS"),sQuery(id+"F3.wireOp",EDGE,"E35.MirrorCS"),subQ9,subQ1,subQ0,subQ8])],"isStart":true})]}),makeQuery(id+"F6.opExtrude","CAP_FACE",FACE,{"disambiguationData":[OSD([subQ7,subQ6,sQuery(id+"F3.wireOp",EDGE,"E5.bottom"),sQuery(id+"F3.wireOp",EDGE,"E5.top"),sQuery(id+"F3.wireOp",EDGE,"E5.left"),sQuery(id+"F3.wireOp",EDGE,"E5.right")])],"isStart":true}),makeQuery(id+"F6.opExtrude","CAP_FACE",FACE,{"disambiguationData":[OSD([sQuery(id+"F3.wireOp",EDGE,"E6.MirrorCS"),subQ5,subQ4,sQuery(id+"F3.wireOp",EDGE,"E15.MirrorCS"),sQuery(id+"F3.wireOp",EDGE,"E16.MirrorCS"),sQuery(id+"F3.wireOp",EDGE,"E17.MirrorCS")])],"isStart":true}),makeQuery(id+"F6.opExtrude","CAP_FACE",FACE,{"disambiguationData":[OSD([sQuery(id+"F3.wireOp",EDGE,"E19.MirrorCS"),subQ3,subQ2,sQuery(id+"F3.wireOp",EDGE,"E28.MirrorCS"),sQuery(id+"F3.wireOp",EDGE,"E29.MirrorCS"),sQuery(id+"F3.wireOp",EDGE,"E30.MirrorCS")])],"isStart":true}),makeQuery(id+"F6.opExtrude","CAP_FACE",FACE,{"disambiguationData":[OSD([sQuery(id+"F3.wireOp",EDGE,"E31.MirrorCS"),sQuery(id+"F3.wireOp",EDGE,"E33.MirrorCS"),sQuery(id+"F3.wireOp",EDGE,"E37.MirrorCS"),subQ1,subQ0,sQuery(id+"F3.wireOp",EDGE,"E41.MirrorCS")])],"isStart":true})]});}
            var sketch = newSketch(context, id + "F17", { "sketchPlane" : qUnion([Q0])});
            skText(sketch, "E78", { "text": "Art Deco", "fontName": "AllertaStencil-Regular.ttf"});
            const initialGuessF17  = {"E78": [-0.025, -0.004, 1, 0, 0.00806]};
            skSetInitialGuess(sketch, initialGuessF17);
            skSolve(sketch);
        }
        {
            var Q0;
            Q0 = qSketchRegion(id + "F17", true);
            extrude(context, id + "F18", {"entities" : qUnion([Q0]), "operationType" : NewBodyOperationType.REMOVE, "oppositeDirection" : true, "depth" : 1 * mm, "offsetDistance" : 25 * mm});
        }
    });